# Revit family: LEGRAND_TOMAS SIN ENCLAVAMIENTO_EMPOTRADAS_IP44_230
name_source: partatom
category: Installations électriques
revit_build: Autodesk Revit 2018 (Build: 20170223_1515(x64)
units: mm (PartAtom-declared; Revit-internal decimal feet)

## family parameters
Conserver l'orientation des annotations = Non
Cote de connecteur circulaire = Utiliser le diamètre
Couper avec des vides une fois chargée = Non
Hôte = Face
Partagée = Non
Point de calcul de pièce = Non
Type d'élément = Normal

## types (17) — shared parameters
Condiciones Generales de Uso = https://export.legrand.com
Description = Toma AL estándar internacional para montaje empotrado o en superficie con accesorio permite la alimentación de aparatos de potencia
Elévation par défaut = 1000 mm
Fabricant = Legrand
Temperatura maxima de instalación = 40°C
Temperatura maxima de uso = 100°C
Temperatura minima de instalación = -20°C
Temperatura minima de uso = -50°C
Tension V = 230 V  50/60 Hz azul
clase de protección IP = IP44
color característico = azul
instalación de empotrar E o de superficie S = empotrar y superficie
tipo de conexión = conexión por tonillo

## per-type parameters (varying)
| type | Dia bouchon | Estándar CEI o NFC | Modèle | RAY BOUCHON | Ray | altura mm | ancho mm | distancia de fijación horizontal mm | distancia de fijación vertical mm | h1 | intensidad A | materia de la caja | numero de polos | posición de la tierra h | profundidad de empotrar mm | profundidad mm | resistencia a los choques IK | sin halogeno |
| base para cuadro à entreejes unificados Hypra   IP44   16 A   200/250 V   2P+T | 55 mm | CEI | 052018 | 27 mm | 27 mm | 84 mm | 84 mm | 70 mm | 70 mm | 50 mm | 16 A | plástico | 3 | 6 | 37 mm | 73 mm  [stored 0.239501 ft] | 09 | Oui |
| base para cuadro à entreejes unificados Hypra   IP44   16 A   200/250 V   3P+T | 55 mm | CEI | 052019 | 27 mm | 27 mm | 84 mm | 84 mm | 70 mm | 70 mm | 50 mm | 16 A | plástico | 4 | 9 | 43 mm | 84 mm | 09 | Oui |
| base para cuadro à entreejes unificados Hypra   IP44   16 A   200/250 V   3P+N+T | 55 mm | CEI | 052020 | 27 mm | 27 mm | 84 mm | 84 mm | 70 mm | 70 mm | 50 mm | 16 A | plástico | 5 | 9 | 43 mm | 80 mm | 09 | Oui |
| base para cuadro Hypra   IP44   16 A   200/250 V   2P+T   plast | 42 mm | CEI | 052022 | 21 mm  [stored 0.0688976 ft] | 21 mm  [stored 0.0688976 ft] | 72 mm | 64 mm | 52 mm | 60 mm | 43 mm | 16 A | plástico | 3 | 6 | 41 mm | 81 mm | 09 | Oui |
| base para cuadro Hypra   IP44   16 A   200/250 V   3P+T   plast | 48 mm | CEI | 052023 | 24 mm | 24 mm | 84 mm | 74 mm | 60 mm | 70 mm | 50 mm | 16 A | plástico | 4 | 9 | 44 mm | 84 mm | 09 | Oui |
| base para cuadro Hypra   IP44   16 A   200/250 V   3P+N+T   plast | 48 mm | CEI | 052024 | 24 mm | 24 mm | 84 mm | 74 mm | 60 mm | 70 mm | 50 mm | 16 A | plástico | 5 | 9 | 44 mm | 88 mm | 09 | Oui |
| base para cuadro Hypra   IP44   16 A   200/250 V   2P+T   métal | 42 mm | CEI | 052032 | 21 mm  [stored 0.0688976 ft] | 21 mm  [stored 0.0688976 ft] | 72 mm | 64 mm | 52 mm | 60 mm | 43 mm | 16 A | metal | 3 | 6 | 41 mm | 81 mm | 10 | Oui |
| base para cuadro Hypra   IP44   16 A   200/250 V   3P+N+T   métal | 48 mm | CEI | 052034 | 24 mm | 24 mm | 84 mm | 74 mm | 60 mm | 70 mm | 50 mm | 16 A | metal | 5 | 9 | 44 mm | 88 mm | 10 | Oui |
| base para cuadro Hypra   IP44   32 A   200/250 V   2P+T   plast | 55 mm | CEI | 052718 | 27 mm | 27 mm | 94 mm | 84 mm | 70 mm | 70 mm | 56 mm | 32 A | plástico | 3 | 6 | 50 mm | 103 mm | 09 | Oui |
| base para cuadro Hypra   IP44   32 A   200/250 V   3P+T   plast | 55 mm | CEI | 052719 | 27 mm | 27 mm | 94 mm | 84 mm | 70 mm | 70 mm | 56 mm | 32 A | plástico | 4 | 9 | 50 mm | 103 mm | 09 | Oui |
| base para cuadro Hypra   IP44   32 A   200/250 V   3P+N+T   plast | 55 mm | CEI | 052720 | 27 mm | 27 mm | 84 mm | 84 mm | 70 mm | 70 mm | 50 mm | 32 A | plástico | 5 | 9 | 52 mm | 108 mm | 09 | Oui |
| base para cuadro Hypra   IP44   32 A   200/250 V   2P+T   métal | 55 mm | CEI | 052732 | 27 mm | 27 mm | 94 mm | 84 mm | 70 mm | 80 mm | 56 mm | 32 A | metal | 5 | 9 | 50 mm | 103 mm | 09 | Oui |
| base para cuadro Hypra   IP44   32 A   200/250 V   3P+T   métal | 55 mm | CEI | 052733 | 27 mm | 27 mm | 94 mm | 84 mm | 70 mm | 80 mm | 56 mm | 32 A | metal | 4 | 9 | 50 mm | 103 mm | 10 | Oui |
| base para cuadro Hypra   IP44   63 A   200/250 V   2P+T   plast | 95 mm | CEI | 053622 | 47 mm | 47 mm | 146 mm  [stored 0.479003 ft] | 146 mm  [stored 0.479003 ft] | 77 mm | 85 mm | 88 mm | 63 A | plástico | 3 | 6 | 98 mm | 168 mm | 09 | Non |
| base para cuadro Hypra   IP44   63 A   200/250 V   3P+T   plast | 69 mm | CEI | 053623 | 34 mm | 34 mm | 106 mm | 106 mm | 77 mm | 85 mm | 64 mm | 63 A | plástico | 4 | 9 | 98 mm | 168 mm | 09 | Non |
| base para cuadro Hypra   IP44   16 A   250 v   2P+T   estandar domestico   plast | 44 mm | NFC | 053903 | 22 mm | 22 mm | 67 mm | 67 mm | 55 mm | 55 mm | 40 mm | 16 A | plástico | 3 | 6 | 19 mm | 49 mm | 09 | Oui |
| base para cuadro Hypra   IP44   16 A   200/250 V   3P+T   métal | 48 mm | CEI | 052033 | 24 mm | 24 mm | 84 mm | 74 mm | 60 mm | 70 mm | 50 mm | 16 A | metal | 4 | 9 | 44 mm | 84 mm | 10 | Oui |

note: [stored X ft] marks values corroborated as IEEE doubles in the binary element streams (Revit-internal decimal feet)
